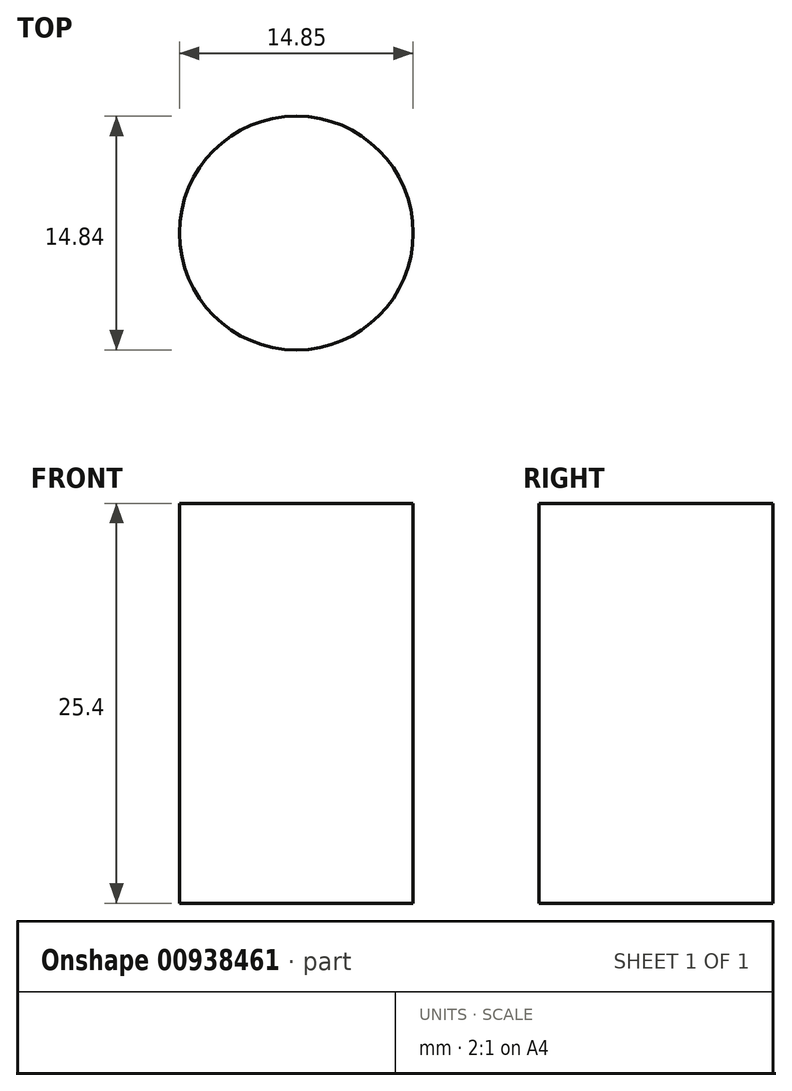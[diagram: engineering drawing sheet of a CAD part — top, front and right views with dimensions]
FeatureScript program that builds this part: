
annotation { "Feature Type Name" : "Feature", "Feature Type Description" : "" }
export const myFeature = defineFeature(function(context is Context, id is Id, definition is map)
    precondition{}
    {
        {
            var Q0;
            Q0=qCreatedBy(makeId("Top.planeOp"),FACE);
            var sketch = newSketch(context, id + "F0", { "sketchPlane" : qUnion([Q0])});
            skCircle(sketch, "E0", {"center": v(3, 0) * mm, "radius": 7.42 * mm});
            skSolve(sketch);
        }
        {
            var Q0;
            Q0 = qSketchRegion(id + "F0", true);
            extrude(context, id + "F1", {"entities" : qUnion([Q0]), "depth" : 25.4 * mm, "offsetDistance" : 25.4 * mm});
        }
    });
